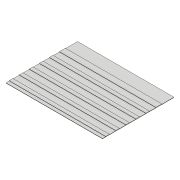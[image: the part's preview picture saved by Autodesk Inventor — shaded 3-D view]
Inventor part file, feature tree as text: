
AUTODESK INVENTOR PART (.ipt)
format: ipt  version: 2017 (Build 210142000, 142)  size: 123,392 bytes
history: native  units: mm
features: extrude x2, sketch x2
ambient origin geometry x8: Origin, YZ Plane, XZ Plane, XY Plane, X Axis, Y Axis, Z Axis, Center Point
bodies: Body1 (feature_tree)
feature tree (4):
  extrude  "Выдавливание2"  Depth=117.5mm
  extrude  "Выдавливание3"  Depth=158.5mm
  sketch  "Эскиз3"
  sketch  "Эскиз4"
